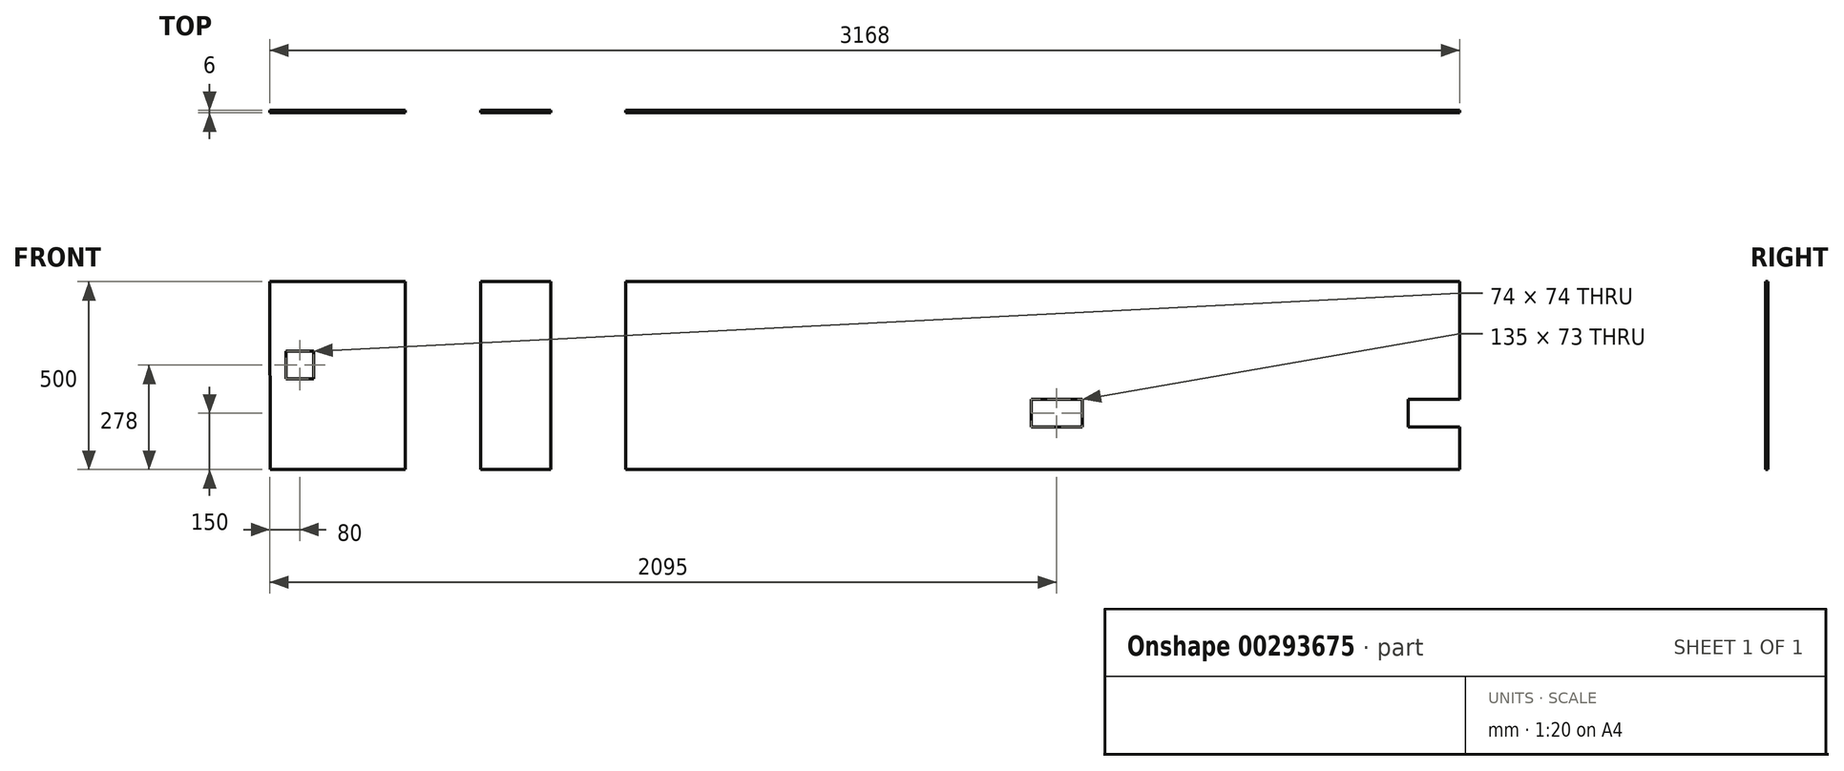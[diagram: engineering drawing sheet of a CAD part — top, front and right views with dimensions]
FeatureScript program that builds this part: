
annotation { "Feature Type Name" : "Feature", "Feature Type Description" : "" }
export const myFeature = defineFeature(function(context is Context, id is Id, definition is map)
    precondition{}
    {
        {
            var Q0;
            Q0=qCreatedBy(makeId("Front.planeOp"),FACE);
            var sketch = newSketch(context, id + "F0", { "sketchPlane" : qUnion([Q0])});
            skLineSegment(sketch, "E0.top", {"start": v(-971, 210) * mm, "end": v(1249, 210) * mm});
            skLineSegment(sketch, "E0.left", {"start": v(-971, -290) * mm, "end": v(-971, 210) * mm});
            skLineSegment(sketch, "E0.right", {"start": v(1249, -290) * mm, "end": v(1249, 210) * mm});
            skLineSegment(sketch, "E1", {"start": v(-971, -290) * mm, "end": v(1249, -290) * mm});
            skLineSegment(sketch, "E2.bottom", {"start": v(108.5, -176.5) * mm, "end": v(243.5, -176.5) * mm});
            skLineSegment(sketch, "E2.top", {"start": v(108.5, -103.5) * mm, "end": v(243.5, -103.5) * mm});
            skLineSegment(sketch, "E2.left", {"start": v(108.5, -103.5) * mm, "end": v(108.5, -176.5) * mm});
            skLineSegment(sketch, "E2.right", {"start": v(243.5, -103.5) * mm, "end": v(243.5, -176.5) * mm});
            skLineSegment(sketch, "E3.bottom", {"start": v(1111, -103.5) * mm, "end": v(1249, -103.5) * mm});
            skLineSegment(sketch, "E3.top", {"start": v(1111, -176.5) * mm, "end": v(1249, -176.5) * mm});
            skLineSegment(sketch, "E3.left", {"start": v(1111, -176.5) * mm, "end": v(1111, -103.5) * mm});
            skLineSegment(sketch, "E4", {"start": v(176, -103.5) * mm, "end": v(176, -176.5) * mm, "construction": true});
            skLineSegment(sketch, "E5", {"start": v(108.5, -140) * mm, "end": v(243.5, -140) * mm, "construction": true});
            skLineSegment(sketch, "E6", {"start": v(1180, -103.5) * mm, "end": v(1180, -176.5) * mm, "construction": true});
            skSolve(sketch);
        }
        {
            var Q0;
            Q0=qCreatedBy(makeId("Front.planeOp"),FACE);
            var sketch = newSketch(context, id + "F1", { "sketchPlane" : qUnion([Q0])});
            skLineSegment(sketch, "E7.bottom", {"start": v(-1171, -290) * mm, "end": v(-1358, -290) * mm});
            skLineSegment(sketch, "E7.top", {"start": v(-1171, 210) * mm, "end": v(-1358, 210) * mm});
            skLineSegment(sketch, "E7.left", {"start": v(-1171, -290) * mm, "end": v(-1171, 210) * mm});
            skLineSegment(sketch, "E7.right", {"start": v(-1358, -290) * mm, "end": v(-1358, 210) * mm});
            skSolve(sketch);
        }
        {
            var Q0;
            Q0=qCreatedBy(makeId("Front.planeOp"),FACE);
            var sketch = newSketch(context, id + "F2", { "sketchPlane" : qUnion([Q0])});
            skLineSegment(sketch, "E8.bottom", {"start": v(-1558, -290) * mm, "end": v(-1917, -290) * mm});
            skLineSegment(sketch, "E8.top", {"start": v(-1558, 210) * mm, "end": v(-1919, 210) * mm});
            skLineSegment(sketch, "E8.left", {"start": v(-1558, -290) * mm, "end": v(-1558, 210) * mm});
            skLineSegment(sketch, "E8.right", {"start": v(-1917, -290) * mm, "end": v(-1919, 210) * mm});
            skLineSegment(sketch, "E9.bottom", {"start": v(-1876, 25) * mm, "end": v(-1802, 25) * mm});
            skLineSegment(sketch, "E9.top", {"start": v(-1876, -49) * mm, "end": v(-1802, -49) * mm});
            skLineSegment(sketch, "E9.left", {"start": v(-1876, 25) * mm, "end": v(-1876, -49) * mm});
            skLineSegment(sketch, "E9.right", {"start": v(-1802, 25) * mm, "end": v(-1802, -49) * mm});
            skLineSegment(sketch, "E10", {"start": v(-1876, -12) * mm, "end": v(-1802, -12) * mm, "construction": true});
            skLineSegment(sketch, "E11", {"start": v(-1839, 25) * mm, "end": v(-1839, -49) * mm, "construction": true});
            skLineSegment(sketch, "E12", {"start": v(-1702, 210) * mm, "end": v(-1702, -290) * mm, "construction": true});
            skSolve(sketch);
        }
        {
            var Q0;
            {var subQ2=sQuery(id+"F0.wireOp",EDGE,"E0.top");Q0=makeQuery(id+"F0.imprint","IMPRINT",FACE,{"disambiguationData":[TD([[makeQuery(id+"F0.imprint","IMPRINT",EDGE,{"derivedFrom":subQ2}),-1.0]])]});}
            extrude(context, id + "F3", {"entities" : qUnion([Q0]), "depth" : 6 * mm});
        }
        {
            var Q0;
            Q0=makeQuery(id+"F1.imprint","IMPRINT",FACE,{"disambiguationData":[TD([[makeQuery(id+"F1.imprint","IMPRINT",EDGE,{"derivedFrom":sQuery(id+"F1.wireOp",EDGE,"E7.bottom")}),-1.0]])]});
            extrude(context, id + "F4", {"entities" : qUnion([Q0]), "depth" : 6 * mm});
        }
        {
            var Q0;
            Q0=makeQuery(id+"F2.imprint","IMPRINT",FACE,{"disambiguationData":[TD([[makeQuery(id+"F2.imprint","IMPRINT",EDGE,{"derivedFrom":sQuery(id+"F2.wireOp",EDGE,"E8.bottom")}),-1.0]])]});
            extrude(context, id + "F5", {"entities" : qUnion([Q0]), "depth" : 6 * mm});
        }
    });
